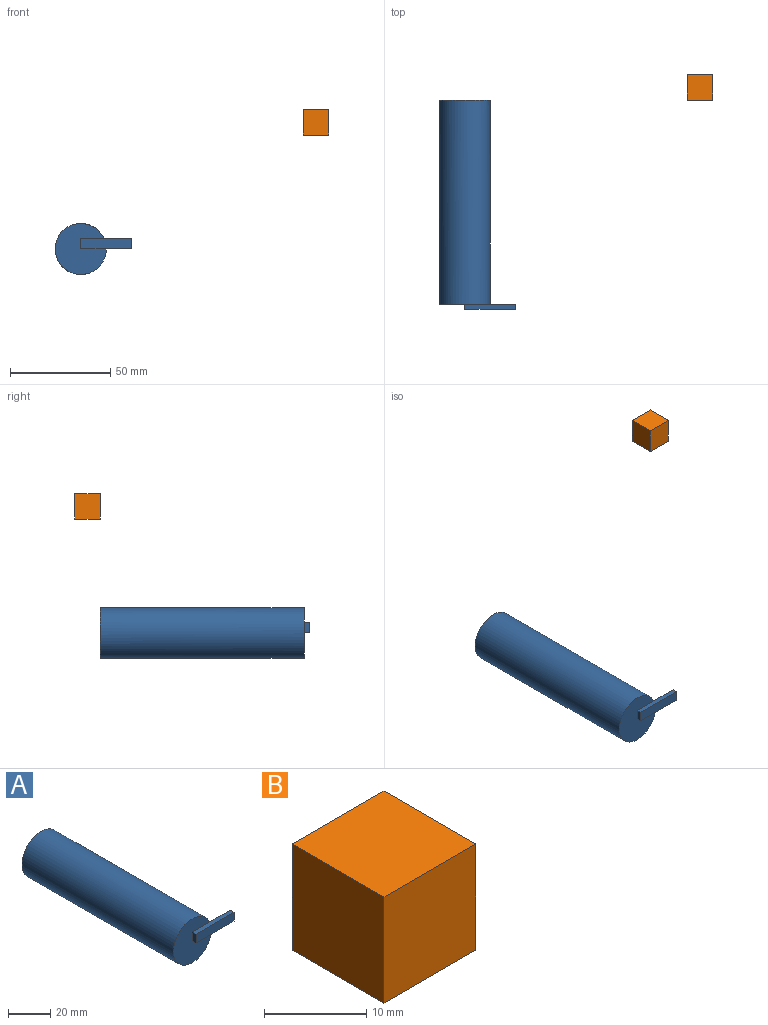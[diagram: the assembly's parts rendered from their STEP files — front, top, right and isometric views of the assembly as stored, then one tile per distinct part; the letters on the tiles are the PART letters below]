
ASSEMBLY  parts=2 mates=1
PART A: 9 faces, bbox 38.1x104.1x25.4 mm
  f0: plane 25.4x25.4mm, normal (0,-1,0), area 444mm2, adj f1,f4,f5,f6
  f1: cylinder r=12.7mm len=101.6mm, axis (0,1,0), area 8107.3mm2, adj f0,f2,f3
  f2: plane 25.4x25.4mm, normal (0,1,0), area 506.7mm2, adj f1
  f3: plane 13.76x5.08mm, normal (0,1,0), area 66.3mm2, adj f1,f4,f6,f7
  f4: plane 25.4x2.54mm, normal (0,0,1), area 64.5mm2, adj f0,f3,f5,f7,f8
  f5: plane 5.08x2.54mm, normal (-1,0,0), area 12.9mm2, adj f0,f4,f6,f8
  f6: plane 25.4x2.54mm, normal (0,0,-1), area 64.5mm2, adj f0,f3,f5,f7,f8
  f7: plane 5.08x2.54mm, normal (1,0,0), area 12.9mm2, adj f3,f4,f6,f8
  f8: plane 25.4x5.08mm, normal (0,-1,0), area 129mm2, adj f4,f5,f6,f7
PART B: 6 faces, bbox 12.7x12.7x12.7 mm
  f0: plane 12.7x12.7mm, normal (0,0,-1), area 161.3mm2, adj f1,f3,f4,f5
  f1: plane 12.7x12.7mm, normal (1,0,0), area 161.3mm2, adj f0,f2,f4,f5
  f2: plane 12.7x12.7mm, normal (0,0,1), area 161.3mm2, adj f1,f3,f4,f5
  f3: plane 12.7x12.7mm, normal (-1,0,0), area 161.3mm2, adj f0,f2,f4,f5
  f4: plane 12.7x12.7mm, normal (0,-1,0), area 161.3mm2, adj f0,f1,f2,f3
  f5: plane 12.7x12.7mm, normal (0,1,0), area 161.3mm2, adj f0,f1,f2,f3
PLACE A t=(-2.51,-228.21,60.3)mm
PLACE B t=(114.73,-215.51,94.85)mm
MATE planar A.f1 <-> B.f4  axis (0,1,0) through (-2.51,-228.21,60.3)mm
